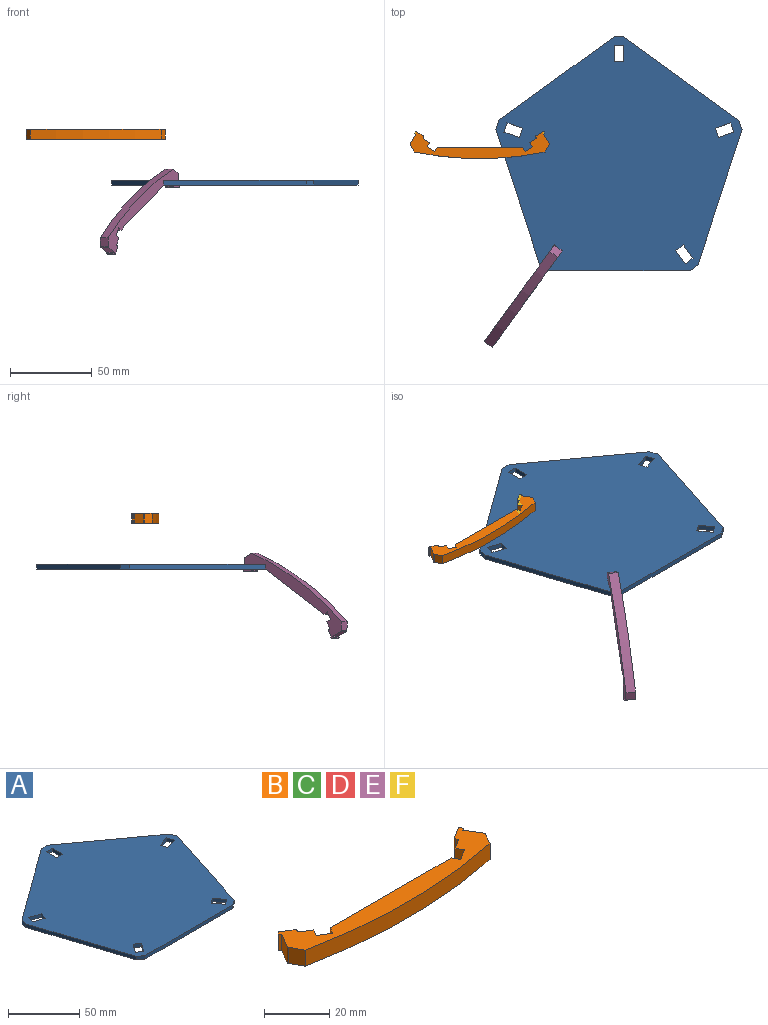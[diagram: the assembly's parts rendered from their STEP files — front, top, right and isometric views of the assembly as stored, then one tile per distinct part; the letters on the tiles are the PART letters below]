
ASSEMBLY  parts=6 mates=2
PART A: 32 faces, bbox 150.7x143.3x3 mm
  f0: plane 9.51x3.09mm, normal (-0.31,0.95,0), area 30mm2, adj f1,f29,f30,f31
  f1: plane 5.71x3mm, normal (0.95,0.31,0), area 18mm2, adj f0,f2,f30,f31
  f2: plane 9.51x3.09mm, normal (0.31,-0.95,0), area 30mm2, adj f1,f29,f30,f31
  f3: plane 8.09x5.88mm, normal (0.81,0.59,0), area 30mm2, adj f4,f24,f30,f31
  f4: plane 4.85x3.53mm, normal (0.59,-0.81,0), area 18mm2, adj f3,f5,f30,f31
  f5: plane 8.09x5.88mm, normal (-0.81,-0.59,0), area 30mm2, adj f4,f24,f30,f31
  f6: plane 8.09x5.88mm, normal (0.81,-0.59,0), area 30mm2, adj f7,f25,f30,f31
  f7: plane 4.85x3.53mm, normal (-0.59,-0.81,0), area 18mm2, adj f6,f8,f30,f31
  f8: plane 8.09x5.88mm, normal (-0.81,0.59,0), area 30mm2, adj f7,f25,f30,f31
  f9: plane 9.51x3.09mm, normal (-0.31,-0.95,0), area 30mm2, adj f10,f26,f30,f31
  f10: plane 5.71x3mm, normal (-0.95,0.31,0), area 18mm2, adj f9,f11,f30,f31
  f11: plane 9.51x3.09mm, normal (0.31,0.95,0), area 30mm2, adj f10,f26,f30,f31
  f12: plane 5.66x3mm, normal (-0.95,0.31,0), area 17.8mm2, adj f13,f27,f30,f31
  f13: plane 82.91x26.94mm, normal (-0.95,-0.31,0), area 261.5mm2, adj f12,f14,f30,f31
  f14: plane 4.81x3.5mm, normal (-0.59,-0.81,0), area 17.8mm2, adj f13,f15,f30,f31
  f15: plane 87.18x3mm, normal (0,-1,0), area 261.5mm2, adj f14,f16,f30,f31
  f16: plane 4.81x3.5mm, normal (0.59,-0.81,0), area 17.8mm2, adj f15,f17,f30,f31
  f17: plane 82.91x26.94mm, normal (0.95,-0.31,0), area 261.5mm2, adj f16,f18,f30,f31
  f18: plane 5.66x3mm, normal (0.95,0.31,0), area 17.8mm2, adj f17,f19,f30,f31
  f19: plane 70.53x51.24mm, normal (0.59,0.81,0), area 261.5mm2, adj f18,f20,f30,f31
  f20: plane 5.95x3mm, normal (0,1,0), area 17.8mm2, adj f19,f27,f30,f31
  f21: plane 6x3mm, normal (0,-1,0), area 18mm2, adj f22,f28,f30,f31
  f22: plane 10x3mm, normal (-1,0,0), area 30mm2, adj f21,f23,f30,f31
  f23: plane 6x3mm, normal (0,1,0), area 18mm2, adj f22,f28,f30,f31
  f24: plane 4.85x3.53mm, normal (-0.59,0.81,0), area 18mm2, adj f3,f5,f30,f31
  f25: plane 4.85x3.53mm, normal (0.59,0.81,0), area 18mm2, adj f6,f8,f30,f31
  f26: plane 5.71x3mm, normal (0.95,-0.31,0), area 18mm2, adj f9,f11,f30,f31
  f27: plane 70.53x51.24mm, normal (-0.59,0.81,0), area 261.5mm2, adj f12,f20,f30,f31
  f28: plane 10x3mm, normal (1,0,0), area 30mm2, adj f21,f23,f30,f31
  f29: plane 5.71x3mm, normal (-0.95,-0.31,0), area 18mm2, adj f0,f2,f30,f31
  f30: plane 150.68x143.31mm, normal (0,0,1), area 15042.2mm2, adj f0,f1,f2,f3,f4,f5,f6,f7
  f31: plane 150.68x143.31mm, normal (0,0,-1), area 15042.2mm2, adj f0,f1,f2,f3,f4,f5,f6,f7
PART B: 32 faces, bbox 85.4x16.7x6 mm
  f0: plane 6x4.78mm, normal (0.88,-0.48,0), area 32.7mm2, adj f1,f29,f30,f31
  f1: cylinder r=0.5mm len=6mm, axis (0,0,-1), area 3.2mm2, adj f0,f2,f30,f31
  f2: plane 6x5.71mm, normal (0.85,0.53,0), area 40.3mm2, adj f1,f3,f30,f31
  f3: plane 6x0.85mm, normal (0.53,-0.85,0), area 6mm2, adj f2,f4,f30,f31
  f4: plane 6x0.85mm, normal (0.85,0.53,0), area 6mm2, adj f3,f5,f30,f31
  f5: cylinder r=0.5mm len=6mm, axis (0,0,-1), area 4.7mm2, adj f4,f6,f30,f31
  f6: plane 6x4.25mm, normal (-0.53,0.85,0), area 30mm2, adj f5,f7,f30,f31
  f7: cylinder r=0.5mm len=6mm, axis (0,0,-1), area 4.7mm2, adj f6,f8,f30,f31
  f8: plane 6x0.43mm, normal (-0.85,-0.53,0), area 3mm2, adj f7,f9,f30,f31
  f9: cylinder r=0.5mm len=6mm, axis (0,0,-1), area 4.7mm2, adj f8,f10,f30,f31
  f10: plane 6x3.83mm, normal (-0.53,0.85,0), area 27mm2, adj f9,f11,f30,f31
  f11: plane 6x2.55mm, normal (-0.85,-0.53,0), area 18mm2, adj f10,f12,f30,f31
  f12: plane 6x4.42mm, normal (-0.53,0.85,0), area 31.2mm2, adj f11,f13,f30,f31
  f13: plane 6x2.55mm, normal (0.85,0.53,0), area 18mm2, adj f12,f14,f30,f31
  f14: plane 52.31x6mm, normal (0,1,0), area 313.9mm2, adj f13,f15,f30,f31
  f15: plane 6x2.55mm, normal (-0.85,0.53,0), area 18mm2, adj f14,f16,f30,f31
  f16: plane 6x4.42mm, normal (0.53,0.85,0), area 31.2mm2, adj f15,f17,f30,f31
  f17: plane 6x2.55mm, normal (0.85,-0.53,0), area 18mm2, adj f16,f18,f30,f31
  f18: plane 6x3.83mm, normal (0.53,0.85,0), area 27mm2, adj f17,f19,f30,f31
  f19: cylinder r=0.5mm len=6mm, axis (0,0,-1), area 4.7mm2, adj f18,f20,f30,f31
  f20: plane 6x0.43mm, normal (0.85,-0.53,0), area 3mm2, adj f19,f21,f30,f31
  f21: cylinder r=0.5mm len=6mm, axis (0,0,-1), area 4.7mm2, adj f20,f22,f30,f31
  f22: plane 6x4.25mm, normal (0.53,0.85,0), area 30mm2, adj f21,f23,f30,f31
  f23: cylinder r=0.5mm len=6mm, axis (0,0,-1), area 4.7mm2, adj f22,f24,f30,f31
  f24: plane 6x0.85mm, normal (-0.85,0.53,0), area 6mm2, adj f23,f25,f30,f31
  f25: plane 6x0.85mm, normal (-0.53,-0.85,0), area 6mm2, adj f24,f26,f30,f31
  f26: plane 6x5.71mm, normal (-0.85,0.53,0), area 40.3mm2, adj f25,f27,f30,f31
  f27: cylinder r=0.5mm len=6mm, axis (0,0,-1), area 3.2mm2, adj f26,f28,f30,f31
  f28: plane 6x4.78mm, normal (-0.88,-0.48,0), area 32.7mm2, adj f27,f29,f30,f31
  f29: cylinder r=198.24mm len=80mm, axis (0,0,-1), area 483.3mm2, adj f0,f28,f30,f31
  f30: plane 85.37x16.68mm, normal (0,0,1), area 587.5mm2, adj f0,f1,f2,f3,f4,f5,f6,f7
  f31: plane 85.37x16.68mm, normal (0,0,-1), area 587.5mm2, adj f0,f1,f2,f3,f4,f5,f6,f7
PART C: same geometry as B
PART D: same geometry as B
PART E: same geometry as B
PART F: same geometry as B
PLACE A at identity
PLACE B t=(-85.22,7.56,28.05)mm
PLACE C t=(-85.22,7.56,28.05)mm
PLACE D t=(-85.22,7.56,28.05)mm
PLACE E rot(axis=(-0.16,0.79,-0.59),122.5deg) t=(-62.4,-80.79,-11.2)mm
PLACE F t=(-85.22,7.56,28.05)mm
MATE planar A.f31 <-> E.f18  axis (0,0,-1) through (0,0,0)mm
MATE planar E.f30 <-> A.f8  axis (0.81,-0.59,0) through (-57.08,-83.66,-12.5)mm
